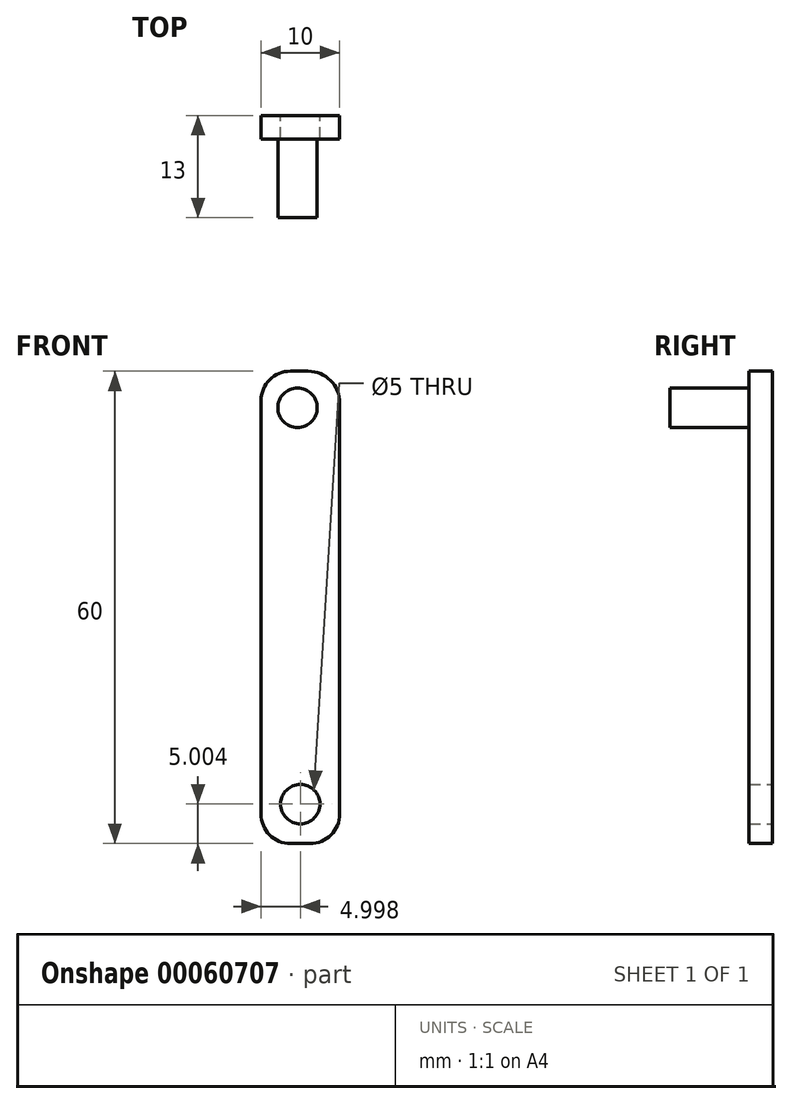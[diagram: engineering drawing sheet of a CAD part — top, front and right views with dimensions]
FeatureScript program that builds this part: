
annotation { "Feature Type Name" : "Feature", "Feature Type Description" : "" }
export const myFeature = defineFeature(function(context is Context, id is Id, definition is map)
    precondition{}
    {
        {
            var Q0;
            Q0=qCreatedBy(makeId("Front.planeOp"),FACE);
            var sketch = newSketch(context, id + "F0", { "sketchPlane" : qUnion([Q0])});
            skLineSegment(sketch, "E0.bottom", {"start": v(-18.35, 30.7) * mm, "end": v(-16.11, 30.7) * mm});
            skLineSegment(sketch, "E0.top", {"start": v(-18.35, -29.3) * mm, "end": v(-15.87, -29.3) * mm});
            skLineSegment(sketch, "E0.left", {"start": v(-22.11, 26.95) * mm, "end": v(-22.11, -25.54) * mm});
            skLineSegment(sketch, "E0.right", {"start": v(-12.11, 26.7) * mm, "end": v(-12.11, -25.54) * mm});
            skPoint(sketch, "E1.visualSharp", {"position": v(-12.11, 30.7) * mm});
            skArc(sketch, "E1.filletArc", {"start": v(-12.11, 26.7) * mm, "mid": v(-13.28, 29.53) * mm, "end": v(-16.11, 30.7) * mm});
            skPoint(sketch, "E2.visualSharp", {"position": v(-22.11, 30.7) * mm});
            skArc(sketch, "E2.filletArc", {"start": v(-18.35, 30.7) * mm, "mid": v(-21.01, 29.6) * mm, "end": v(-22.11, 26.95) * mm});
            skPoint(sketch, "E3.visualSharp", {"position": v(-22.11, -29.3) * mm});
            skArc(sketch, "E3.filletArc", {"start": v(-22.11, -25.54) * mm, "mid": v(-21.01, -28.2) * mm, "end": v(-18.35, -29.3) * mm});
            skPoint(sketch, "E4.visualSharp", {"position": v(-12.11, -29.3) * mm});
            skArc(sketch, "E4.filletArc", {"start": v(-15.87, -29.3) * mm, "mid": v(-13.21, -28.2) * mm, "end": v(-12.11, -25.54) * mm});
            skCircle(sketch, "E5", {"center": v(-17.47, 26.06) * mm, "radius": 2.5 * mm});
            skCircle(sketch, "E6", {"center": v(-17.11, -24.3) * mm, "radius": 2.5 * mm});
            skSolve(sketch);
        }
        {
            var Q0;
            Q0=makeQuery(id+"F0.imprint","IMPRINT",FACE,{"disambiguationData":[TD([[makeQuery(id+"F0.imprint","IMPRINT",EDGE,{"derivedFrom":sQuery(id+"F0.wireOp",EDGE,"E0.bottom")}),-1.0]])]});
            var Q1;
            Q1=makeQuery(id+"F0.imprint","IMPRINT",FACE,{"disambiguationData":[TD([[makeQuery(id+"F0.imprint","IMPRINT",EDGE,{"derivedFrom":sQuery(id+"F0.wireOp",EDGE,"E6")}),-1.0]])]});
            extrude(context, id + "F1", {"entities" : qUnion([Q0, Q1]), "depth" : 3 * mm});
        }
        {
            var Q0;
            Q0=makeQuery(id+"F0.imprint","IMPRINT",FACE,{"disambiguationData":[TD([[makeQuery(id+"F0.imprint","IMPRINT",EDGE,{"derivedFrom":sQuery(id+"F0.wireOp",EDGE,"E5")}),1.0]])]});
            extrude(context, id + "F2", {"entities" : qUnion([Q0]), "operationType" : NewBodyOperationType.ADD, "depth" : 13 * mm});
        }
    });
